# Revit family: Gira_208900
name_source: partatom
category: Elektroinstallationen
revit_build: Autodesk Revit 2017 (Build: 20160225_1515(x64)
units: mm (PartAtom-declared; Revit-internal decimal feet)

## family parameters
Basisbauteil = Fläche
Beim Laden mit Abzugskörper schneiden = Nein
Bemaßung runder Anschluss = Durchmesser verwenden
Beschriftungsausrichtung beibehalten = Nein
Gemeinsam genutzt = Nein
Raumberechnungspunkt = Nein
Teiletyp = Normal

## types (1)
- Gira_208900
    BIM = https://media.stage.bim.site X1 REG KNX.rfa
    Beschreibung = Gira S1 DRA KNX,Gira S1,,DRA,Features:,- Secure access via Gira Smart Home app, HomeServer iOS app and Gira security system iOS or Android app.,- Secure remote access to web-based visualisations.,- Secure remote maintenance and remote programming of the Gira HomeServer, Gira G1, Gira X1, Gira L1, Gira DCS IP data interface, Gira Alarm Connect security system and Gira KNX IP router.,- Secure remote programming via the Gira HomeServer experts.,- Secure remote programming via the Gira Project Assistant (GPA).,- Secure remote maintenance and remote programming of KNX projects using ETS4 or ETS5. The programming and diagnosis is supported via group and bus monitor.,- Secure remote access to HTML pages in the smart home network (e.g. camera, NAS, router, switch).,- Secure data transfer courtesy of SSL TLS encryption.,- Portal server is located in Germany and is subject to German laws on data.,- Independence from internet provider and routers used. Secure remote access even with IPv6 Dual Stack Lite - (e.g. with Unitymedia), LTE, or UMTS connections.,- Management of access to the secure connections via KNX communication objects, Gira X1 ap, Gira HomeServer app, and QuadClient.,- Status signalling of the secure connections via KNX communication objects, Gira X1 ap, Gira HomeServer app, and QuadClient.,- Send notifications via e-mail. An attachment can be added to the email, as an option.,- Send notifications by text message or voice call via the chargeable, additional service sms77 or MessageBird.,- Notification triggers can be configured individually (filters, conditions, hysteresis).,- Supports up to 50 notifications.,- Optimised KNX IP communication, for mobile or very slow connections.,- Supports the accelerated transfer of the ETS to KNXnet IP devices via a direct KNX IP connection.,- Two RJ45 sockets with switch functionality support simple loop-through of the patch cable.,- Quick and convenient Gira S1 start-up via the Gira device portal.,- 2 GB of data each month.,- Unlimited operating life and 5 years' guaranteed server operation.,- Functional extensions and updates via firmware and software updates.,- Firmware update is performed via the Gira Project Assistant (GPA).,- Hardware prepared for KNX Secure. Future firmware update required.,,Notes :,- Supply via external DC 24 V.,- microSD card not included in delivery.
    Bus connection included = Nein
    Bus system KNX = Ja
    Bus system KNX radio = Nein
    Bus system LON = Nein
    Bus system Powernet = Nein
    Bus system radio frequent = Nein
    Central functional unit for senders/actuators = Ja
    Colour = Red
    Data sheet = https://katalog.gira.de
    Degree of protection (IP) = IP21
    GTIN = 4010337035374
    HAN = 208900
    Hersteller = Gira
    IR sensor = Nein
    Integrated DCF77 receiver = Nein
    Logic object = Ja
    Material = Other
    Material quality = Other
    Model = Other
    Mounting method = DRA (DIN-rail adapter)
    Other bus systems = Other
    Presence button = Nein
    Productwebsite = http://katalog.gira.de
    Radio frequent bidirectional = Nein
    Status-LED = Ja
    Surface finishing = Not applicable
    Surface protection = Other
    Temperature controller = Ja
    Transparent = Nein
    Typname = Gira S1 KNX DRA
    URL = https://www.gira.de
    Vorgabe-Ansicht = 1219 mm
    Width in number of modular spacings = 2
    With anti-theft/dismantling protection = Ja
    With display = Ja
    With label area = Nein

## geometry (parser evidence)
native form markers: Sweep x2
no freeform markers — native parametric forms only
